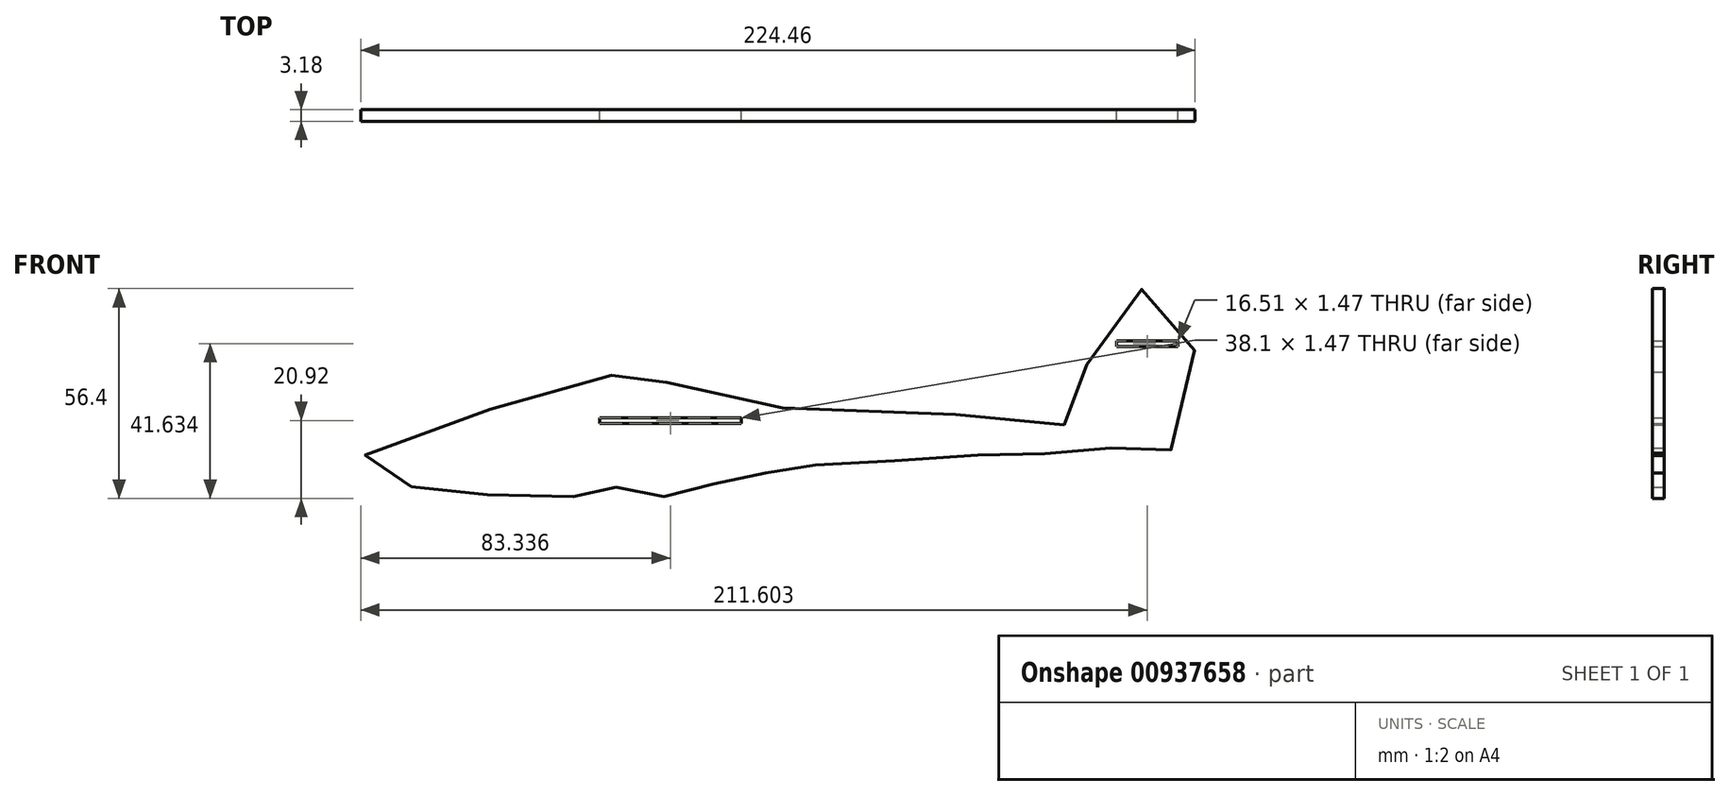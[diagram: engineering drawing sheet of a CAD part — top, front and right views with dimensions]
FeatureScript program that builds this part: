
annotation { "Feature Type Name" : "Feature", "Feature Type Description" : "" }
export const myFeature = defineFeature(function(context is Context, id is Id, definition is map)
    precondition{}
    {
        {
            var Q0;
            Q0=qCreatedBy(makeId("Front.planeOp"),FACE);
            var sketch = newSketch(context, id + "F0", { "sketchPlane" : qUnion([Q0])});
            skLineSegment(sketch, "E0.bottom", {"start": v(114.3, 50.8) * mm, "end": v(-114.3, 50.8) * mm, "construction": true});
            skLineSegment(sketch, "E0.top", {"start": v(114.3, -50.8) * mm, "end": v(-114.3, -50.8) * mm, "construction": true});
            skLineSegment(sketch, "E0.left", {"start": v(114.3, 50.8) * mm, "end": v(114.3, -50.8) * mm, "construction": true});
            skLineSegment(sketch, "E0.right", {"start": v(-114.3, 50.8) * mm, "end": v(-114.3, -50.8) * mm, "construction": true});
            skPoint(sketch, "E0.middle", {"position": v(0, 0) * mm});
            skFitSpline(sketch, "E1", {"points": [v(-95.88, -17.8) * mm, v(-74.85, -20.03) * mm, v(-50.6, -20.24) * mm, v(-45.54, -18.38) * mm, v(-36.51, -18.4) * mm, v(-28.96, -20.2) * mm, v(-19.04, -20.16) * mm, v(-10.48, -14.64) * mm, v(0, -14.06) * mm, v(7, -12.44) * mm, v(24.95, -11.72) * mm, v(49.57, -9.37) * mm, v(69.93, -9.34) * mm, v(81.22, -7.96) * mm, v(100.29, -7.94) * mm, v(109.36, -7.08) * mm, v(111.56, 31.12) * mm, v(91.83, 29.95) * mm, v(82.6, 0) * mm, v(74.27, 0) * mm, v(-10.46, 5.2) * mm, v(-34.81, 12.94) * mm, v(-50.83, 9.51) * mm, v(-109.37, -10.75) * mm, v(-95.88, -17.8) * mm]});
            skPoint(sketch, "E2", {"position": v(-64.29, 5.84) * mm});
            skPoint(sketch, "E3", {"position": v(-85.37, 0) * mm});
            skLineSegment(sketch, "E4.bottom", {"start": v(-7.08, 0.74) * mm, "end": v(-45.18, 0.74) * mm});
            skLineSegment(sketch, "E4.top", {"start": v(-7.08, -0.74) * mm, "end": v(-45.18, -0.74) * mm});
            skLineSegment(sketch, "E4.left", {"start": v(-7.08, 0.74) * mm, "end": v(-7.08, -0.74) * mm});
            skLineSegment(sketch, "E4.right", {"start": v(-45.18, 0.74) * mm, "end": v(-45.18, -0.74) * mm});
            skPoint(sketch, "E4.middle", {"position": v(-26.13, 0) * mm});
            skLineSegment(sketch, "E5.bottom", {"start": v(93.88, 21.45) * mm, "end": v(110.39, 21.45) * mm});
            skLineSegment(sketch, "E5.top", {"start": v(93.88, 19.98) * mm, "end": v(110.39, 19.98) * mm});
            skLineSegment(sketch, "E5.left", {"start": v(93.88, 21.45) * mm, "end": v(93.88, 19.98) * mm});
            skLineSegment(sketch, "E5.right", {"start": v(110.39, 21.45) * mm, "end": v(110.39, 19.98) * mm});
            skSolve(sketch);
        }
        {
            var Q0;
            Q0 = qSketchRegion(id + "F0", true);
            extrude(context, id + "F1", {"entities" : qUnion([Q0]), "depth" : 3.17 * mm, "offsetDistance" : 25.4 * mm});
        }
    });
